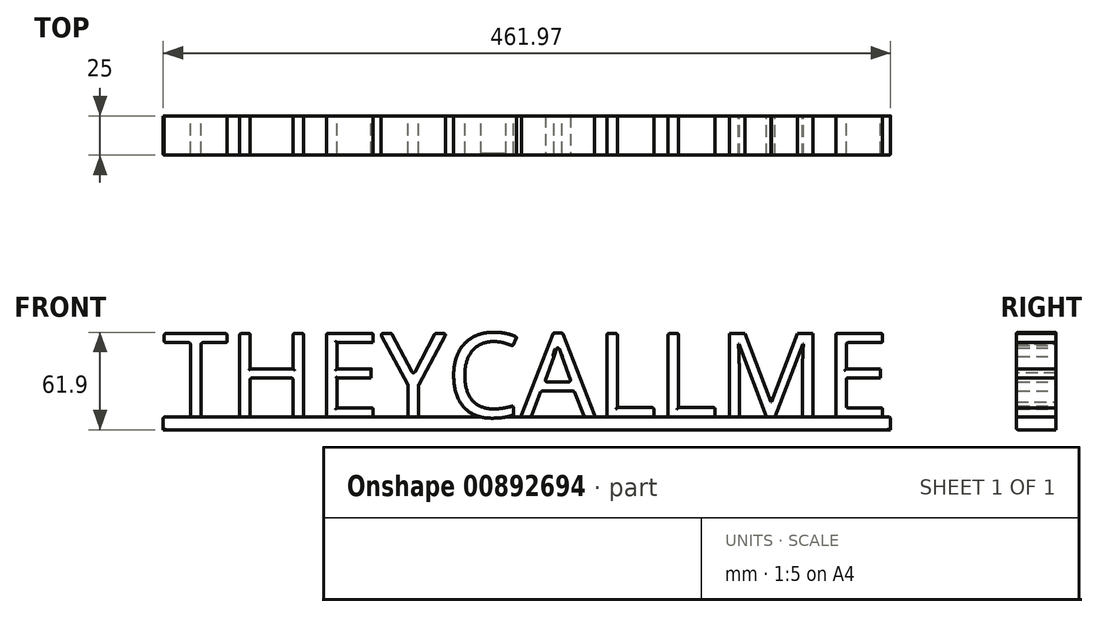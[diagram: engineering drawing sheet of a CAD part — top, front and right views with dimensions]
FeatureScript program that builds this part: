
annotation { "Feature Type Name" : "Feature", "Feature Type Description" : "" }
export const myFeature = defineFeature(function(context is Context, id is Id, definition is map)
    precondition{}
    {
        {
            var Q0;
            Q0=qCreatedBy(makeId("Front.planeOp"),FACE);
            var sketch = newSketch(context, id + "F0", { "sketchPlane" : qUnion([Q0])});
            skText(sketch, "E0", { "text": "THEYCALLME", "fontName": "NotoSans-Regular.ttf"});
            skLineSegment(sketch, "E1.bottom", {"start": v(-74, 3.83) * mm, "end": v(387.97, 3.83) * mm});
            skLineSegment(sketch, "E1.top", {"start": v(-74, -4.21) * mm, "end": v(387.97, -4.21) * mm});
            skLineSegment(sketch, "E1.left", {"start": v(-74, 3.83) * mm, "end": v(-74, -4.21) * mm});
            skLineSegment(sketch, "E1.right", {"start": v(387.97, 3.83) * mm, "end": v(387.97, -4.21) * mm});
            const initialGuessF0  = {"E0": [-0.074, 0.00383, 1, 0, 0.05356]};
            skSetInitialGuess(sketch, initialGuessF0);
            skSolve(sketch);
        }
        {
            var Q0;
            {var subQ0=sQuery(id+"F0.wireOp",EDGE,"E0.sketch_text.stroke-1");Q0=makeQuery(id+"F0.imprint","IMPRINT",FACE,{"disambiguationData":[TD([[makeQuery(id+"F0.imprint","IMPRINT",EDGE,{"derivedFrom":subQ0}),-1.0]])]});}
            var Q1;
            {var subQ0=sQuery(id+"F0.wireOp",EDGE,"E0.sketch_text.stroke-21");Q1=makeQuery(id+"F0.imprint","IMPRINT",FACE,{"disambiguationData":[TD([[makeQuery(id+"F0.imprint","IMPRINT",EDGE,{"derivedFrom":subQ0}),-1.0]])]});}
            var Q2;
            Q2=makeQuery(id+"F0.imprint","IMPRINT",FACE,{"disambiguationData":[TD([[makeQuery(id+"F0.imprint","IMPRINT",EDGE,{"derivedFrom":sQuery(id+"F0.wireOp",EDGE,"E0.sketch_text.stroke-32")}),-1.0]])]});
            var Q3;
            Q3=makeQuery(id+"F0.imprint","IMPRINT",FACE,{"disambiguationData":[TD([[makeQuery(id+"F0.imprint","IMPRINT",EDGE,{"derivedFrom":sQuery(id+"F0.wireOp",EDGE,"E0.sketch_text.stroke-41")}),-1.0]])]});
            var Q4;
            {var subQ0=sQuery(id+"F0.wireOp",EDGE,"E0.sketch_text.stroke-70");Q4=makeQuery(id+"F0.imprint","IMPRINT",FACE,{"disambiguationData":[TD([[makeQuery(id+"F0.imprint","IMPRINT",EDGE,{"derivedFrom":subQ0}),-1.0]])]});}
            var Q5;
            {var subQ1=sQuery(id+"F0.wireOp",EDGE,"E0.sketch_text.stroke-76");Q5=makeQuery(id+"F0.imprint","IMPRINT",FACE,{"disambiguationData":[TD([[makeQuery(id+"F0.imprint","IMPRINT",EDGE,{"derivedFrom":subQ1}),-1.0]])]});}
            var Q6;
            {var subQ1=sQuery(id+"F0.wireOp",EDGE,"E0.sketch_text.stroke-101");Q6=makeQuery(id+"F0.imprint","IMPRINT",FACE,{"disambiguationData":[TD([[makeQuery(id+"F0.imprint","IMPRINT",EDGE,{"derivedFrom":subQ1}),-1.0]])]});}
            var Q7;
            Q7=makeQuery(id+"F0.imprint","IMPRINT",FACE,{"disambiguationData":[TD([[makeQuery(id+"F0.imprint","IMPRINT",EDGE,{"derivedFrom":sQuery(id+"F0.wireOp",EDGE,"E0.sketch_text.stroke-132")}),-1.0]])]});
            var Q8;
            {var subQ1=sQuery(id+"F0.wireOp",EDGE,"E0.sketch_text.stroke-147");Q8=makeQuery(id+"F0.imprint","IMPRINT",FACE,{"disambiguationData":[TD([[makeQuery(id+"F0.imprint","IMPRINT",EDGE,{"derivedFrom":subQ1}),-1.0]])]});}
            var Q9;
            {var subQ1=sQuery(id+"F0.wireOp",EDGE,"E0.sketch_text.stroke-9");Q9=makeQuery(id+"F0.imprint","IMPRINT",FACE,{"disambiguationData":[TD([[makeQuery(id+"F0.imprint","IMPRINT",EDGE,{"derivedFrom":subQ1}),-1.0]])]});}
            var Q10;
            {var subQ0=sQuery(id+"F0.wireOp",EDGE,"E0.sketch_text.stroke-48");Q10=makeQuery(id+"F0.imprint","IMPRINT",FACE,{"disambiguationData":[TD([[makeQuery(id+"F0.imprint","IMPRINT",EDGE,{"derivedFrom":subQ0}),-1.0]])]});}
            var Q11;
            Q11=makeQuery(id+"F0.imprint","IMPRINT",FACE,{"disambiguationData":[TD([[makeQuery(id+"F0.imprint","IMPRINT",EDGE,{"derivedFrom":sQuery(id+"F0.wireOp",EDGE,"E0.sketch_text.stroke-112")}),-1.0]])]});
            var Q12;
            {var subQ0=sQuery(id+"F0.wireOp",EDGE,"E0.sketch_text.stroke-135");var subQ1=sQuery(id+"F0.wireOp",EDGE,"E0.sketch_text.stroke-134");var subQ2=makeQuery(id+"F0.imprint","INTERSECT",VERTEX,{"derivedFrom":[subQ1,subQ0]});Q12=makeQuery(id+"F0.imprint","IMPRINT",FACE,{"disambiguationData":[TD([[makeQuery(id+"F0.imprint","IMPRINT",EDGE,{"disambiguationData":[TD([[subQ2,1.0]])],"derivedFrom":subQ1}),-1.0]])]});}
            var Q13;
            {var subQ2=sQuery(id+"F0.wireOp",EDGE,"E0.sketch_text.stroke-159");Q13=makeQuery(id+"F0.imprint","IMPRINT",FACE,{"disambiguationData":[TD([[makeQuery(id+"F0.imprint","IMPRINT",EDGE,{"derivedFrom":subQ2}),-1.0]])]});}
            var Q14;
            {var subQ3=sQuery(id+"F0.wireOp",EDGE,"E0.sketch_text.stroke-177");Q14=makeQuery(id+"F0.imprint","IMPRINT",FACE,{"disambiguationData":[TD([[makeQuery(id+"F0.imprint","IMPRINT",EDGE,{"derivedFrom":subQ3}),-1.0]])]});}
            var Q15;
            {var subQ1=sQuery(id+"F0.wireOp",EDGE,"E0.sketch_text.stroke-57");Q15=makeQuery(id+"F0.imprint","IMPRINT",FACE,{"disambiguationData":[TD([[makeQuery(id+"F0.imprint","IMPRINT",EDGE,{"derivedFrom":subQ1}),-1.0]])]});}
            var Q16;
            {var subQ1=sQuery(id+"F0.wireOp",EDGE,"E0.sketch_text.stroke-82");Q16=makeQuery(id+"F0.imprint","IMPRINT",FACE,{"disambiguationData":[TD([[makeQuery(id+"F0.imprint","IMPRINT",EDGE,{"derivedFrom":subQ1}),-1.0]])]});}
            var Q17;
            {var subQ1=sQuery(id+"F0.wireOp",EDGE,"E0.sketch_text.stroke-117");Q17=makeQuery(id+"F0.imprint","IMPRINT",FACE,{"disambiguationData":[TD([[makeQuery(id+"F0.imprint","IMPRINT",EDGE,{"derivedFrom":subQ1}),-1.0]])]});}
            extrude(context, id + "F1", {"entities" : qUnion([Q0, Q1, Q2, Q3, Q4, Q5, Q6, Q7, Q8, Q9, Q10, Q11, Q12, Q13, Q14, Q15, Q16, Q17]), "depth" : 25 * mm, "offsetDistance" : 25 * mm});
        }
        {
            var Q0;
            Q0=makeQuery(id+"F1.opExtrude","CAP_FACE",FACE,{"disambiguationData":[OSD([sQuery(id+"F0.wireOp",EDGE,"E0.sketch_text.stroke-1"),sQuery(id+"F0.wireOp",EDGE,"E0.sketch_text.stroke-2"),sQuery(id+"F0.wireOp",EDGE,"E0.sketch_text.stroke-3"),sQuery(id+"F0.wireOp",EDGE,"E0.sketch_text.stroke-4"),sQuery(id+"F0.wireOp",EDGE,"E0.sketch_text.stroke-5"),sQuery(id+"F0.wireOp",EDGE,"E0.sketch_text.stroke-6"),sQuery(id+"F0.wireOp",EDGE,"E0.sketch_text.stroke-7"),sQuery(id+"F0.wireOp",EDGE,"E1.bottom")])],"isStart":false});
            var Q1;
            Q1=makeQuery(id+"F1.opExtrude","CAP_FACE",FACE,{"disambiguationData":[OSD([sQuery(id+"F0.wireOp",EDGE,"E0.sketch_text.stroke-9"),sQuery(id+"F0.wireOp",EDGE,"E0.sketch_text.stroke-10"),sQuery(id+"F0.wireOp",EDGE,"E0.sketch_text.stroke-11"),sQuery(id+"F0.wireOp",EDGE,"E0.sketch_text.stroke-13"),sQuery(id+"F0.wireOp",EDGE,"E0.sketch_text.stroke-14"),sQuery(id+"F0.wireOp",EDGE,"E0.sketch_text.stroke-15"),sQuery(id+"F0.wireOp",EDGE,"E0.sketch_text.stroke-16"),sQuery(id+"F0.wireOp",EDGE,"E0.sketch_text.stroke-17"),sQuery(id+"F0.wireOp",EDGE,"E0.sketch_text.stroke-18"),sQuery(id+"F0.wireOp",EDGE,"E0.sketch_text.stroke-19"),sQuery(id+"F0.wireOp",EDGE,"E1.bottom")])],"isStart":false});
            var Q2;
            Q2=makeQuery(id+"F1.opExtrude","CAP_FACE",FACE,{"disambiguationData":[OSD([sQuery(id+"F0.wireOp",EDGE,"E0.sketch_text.stroke-21"),sQuery(id+"F0.wireOp",EDGE,"E0.sketch_text.stroke-22"),sQuery(id+"F0.wireOp",EDGE,"E0.sketch_text.stroke-23"),sQuery(id+"F0.wireOp",EDGE,"E0.sketch_text.stroke-24"),sQuery(id+"F0.wireOp",EDGE,"E0.sketch_text.stroke-25"),sQuery(id+"F0.wireOp",EDGE,"E0.sketch_text.stroke-26"),sQuery(id+"F0.wireOp",EDGE,"E0.sketch_text.stroke-27"),sQuery(id+"F0.wireOp",EDGE,"E0.sketch_text.stroke-28"),sQuery(id+"F0.wireOp",EDGE,"E0.sketch_text.stroke-29"),sQuery(id+"F0.wireOp",EDGE,"E0.sketch_text.stroke-30"),sQuery(id+"F0.wireOp",EDGE,"E0.sketch_text.stroke-31"),sQuery(id+"F0.wireOp",EDGE,"E1.bottom")])],"isStart":false});
            var Q3;
            Q3=makeQuery(id+"F1.opExtrude","CAP_FACE",FACE,{"disambiguationData":[OSD([sQuery(id+"F0.wireOp",EDGE,"E0.sketch_text.stroke-32"),sQuery(id+"F0.wireOp",EDGE,"E0.sketch_text.stroke-33"),sQuery(id+"F0.wireOp",EDGE,"E0.sketch_text.stroke-34"),sQuery(id+"F0.wireOp",EDGE,"E0.sketch_text.stroke-35"),sQuery(id+"F0.wireOp",EDGE,"E0.sketch_text.stroke-37"),sQuery(id+"F0.wireOp",EDGE,"E0.sketch_text.stroke-38"),sQuery(id+"F0.wireOp",EDGE,"E0.sketch_text.stroke-39"),sQuery(id+"F0.wireOp",EDGE,"E0.sketch_text.stroke-40"),sQuery(id+"F0.wireOp",EDGE,"E1.bottom")])],"isStart":false});
            var Q4;
            Q4=makeQuery(id+"F1.opExtrude","CAP_FACE",FACE,{"disambiguationData":[OSD([sQuery(id+"F0.wireOp",EDGE,"E0.sketch_text.stroke-41"),sQuery(id+"F0.wireOp",EDGE,"E0.sketch_text.stroke-42"),sQuery(id+"F0.wireOp",EDGE,"E0.sketch_text.stroke-43"),sQuery(id+"F0.wireOp",EDGE,"E0.sketch_text.stroke-44"),sQuery(id+"F0.wireOp",EDGE,"E0.sketch_text.stroke-45"),sQuery(id+"F0.wireOp",EDGE,"E0.sketch_text.stroke-46"),sQuery(id+"F0.wireOp",EDGE,"E0.sketch_text.stroke-47"),sQuery(id+"F0.wireOp",EDGE,"E0.sketch_text.stroke-48"),sQuery(id+"F0.wireOp",EDGE,"E0.sketch_text.stroke-49"),sQuery(id+"F0.wireOp",EDGE,"E0.sketch_text.stroke-50"),sQuery(id+"F0.wireOp",EDGE,"E0.sketch_text.stroke-51"),sQuery(id+"F0.wireOp",EDGE,"E0.sketch_text.stroke-52"),sQuery(id+"F0.wireOp",EDGE,"E0.sketch_text.stroke-53"),sQuery(id+"F0.wireOp",EDGE,"E0.sketch_text.stroke-54"),sQuery(id+"F0.wireOp",EDGE,"E0.sketch_text.stroke-55"),sQuery(id+"F0.wireOp",EDGE,"E0.sketch_text.stroke-56")])],"isStart":false});
            var Q5;
            Q5=makeQuery(id+"F1.opExtrude","CAP_FACE",FACE,{"disambiguationData":[OSD([sQuery(id+"F0.wireOp",EDGE,"E0.sketch_text.stroke-57"),sQuery(id+"F0.wireOp",EDGE,"E0.sketch_text.stroke-58"),sQuery(id+"F0.wireOp",EDGE,"E0.sketch_text.stroke-59"),sQuery(id+"F0.wireOp",EDGE,"E0.sketch_text.stroke-61"),sQuery(id+"F0.wireOp",EDGE,"E0.sketch_text.stroke-62"),sQuery(id+"F0.wireOp",EDGE,"E0.sketch_text.stroke-63"),sQuery(id+"F0.wireOp",EDGE,"E0.sketch_text.stroke-65"),sQuery(id+"F0.wireOp",EDGE,"E0.sketch_text.stroke-66"),sQuery(id+"F0.wireOp",EDGE,"E0.sketch_text.stroke-67"),sQuery(id+"F0.wireOp",EDGE,"E0.sketch_text.stroke-68"),sQuery(id+"F0.wireOp",EDGE,"E0.sketch_text.stroke-69"),sQuery(id+"F0.wireOp",EDGE,"E1.bottom")])],"isStart":false});
            var Q6;
            Q6=makeQuery(id+"F1.opExtrude","CAP_FACE",FACE,{"disambiguationData":[OSD([sQuery(id+"F0.wireOp",EDGE,"E0.sketch_text.stroke-70"),sQuery(id+"F0.wireOp",EDGE,"E0.sketch_text.stroke-71"),sQuery(id+"F0.wireOp",EDGE,"E0.sketch_text.stroke-72"),sQuery(id+"F0.wireOp",EDGE,"E0.sketch_text.stroke-73"),sQuery(id+"F0.wireOp",EDGE,"E0.sketch_text.stroke-74"),sQuery(id+"F0.wireOp",EDGE,"E1.bottom")])],"isStart":false});
            var Q7;
            Q7=makeQuery(id+"F1.opExtrude","CAP_FACE",FACE,{"disambiguationData":[OSD([sQuery(id+"F0.wireOp",EDGE,"E0.sketch_text.stroke-76"),sQuery(id+"F0.wireOp",EDGE,"E0.sketch_text.stroke-77"),sQuery(id+"F0.wireOp",EDGE,"E0.sketch_text.stroke-78"),sQuery(id+"F0.wireOp",EDGE,"E0.sketch_text.stroke-79"),sQuery(id+"F0.wireOp",EDGE,"E0.sketch_text.stroke-80"),sQuery(id+"F0.wireOp",EDGE,"E1.bottom")])],"isStart":false});
            var Q8;
            Q8=makeQuery(id+"F1.opExtrude","CAP_FACE",FACE,{"disambiguationData":[OSD([sQuery(id+"F0.wireOp",EDGE,"E0.sketch_text.stroke-82"),sQuery(id+"F0.wireOp",EDGE,"E0.sketch_text.stroke-83"),sQuery(id+"F0.wireOp",EDGE,"E0.sketch_text.stroke-84"),sQuery(id+"F0.wireOp",EDGE,"E0.sketch_text.stroke-85"),sQuery(id+"F0.wireOp",EDGE,"E0.sketch_text.stroke-87"),sQuery(id+"F0.wireOp",EDGE,"E0.sketch_text.stroke-88"),sQuery(id+"F0.wireOp",EDGE,"E0.sketch_text.stroke-89"),sQuery(id+"F0.wireOp",EDGE,"E0.sketch_text.stroke-90"),sQuery(id+"F0.wireOp",EDGE,"E0.sketch_text.stroke-91"),sQuery(id+"F0.wireOp",EDGE,"E0.sketch_text.stroke-92"),sQuery(id+"F0.wireOp",EDGE,"E0.sketch_text.stroke-93"),sQuery(id+"F0.wireOp",EDGE,"E0.sketch_text.stroke-95"),sQuery(id+"F0.wireOp",EDGE,"E0.sketch_text.stroke-96"),sQuery(id+"F0.wireOp",EDGE,"E0.sketch_text.stroke-97"),sQuery(id+"F0.wireOp",EDGE,"E0.sketch_text.stroke-98"),sQuery(id+"F0.wireOp",EDGE,"E1.bottom")])],"isStart":false});
            var Q9;
            Q9=makeQuery(id+"F1.opExtrude","CAP_FACE",FACE,{"disambiguationData":[OSD([sQuery(id+"F0.wireOp",EDGE,"E0.sketch_text.stroke-101"),sQuery(id+"F0.wireOp",EDGE,"E0.sketch_text.stroke-102"),sQuery(id+"F0.wireOp",EDGE,"E0.sketch_text.stroke-103"),sQuery(id+"F0.wireOp",EDGE,"E0.sketch_text.stroke-104"),sQuery(id+"F0.wireOp",EDGE,"E0.sketch_text.stroke-105"),sQuery(id+"F0.wireOp",EDGE,"E0.sketch_text.stroke-106"),sQuery(id+"F0.wireOp",EDGE,"E0.sketch_text.stroke-107"),sQuery(id+"F0.wireOp",EDGE,"E0.sketch_text.stroke-108"),sQuery(id+"F0.wireOp",EDGE,"E0.sketch_text.stroke-109"),sQuery(id+"F0.wireOp",EDGE,"E0.sketch_text.stroke-110"),sQuery(id+"F0.wireOp",EDGE,"E0.sketch_text.stroke-111"),sQuery(id+"F0.wireOp",EDGE,"E1.bottom")])],"isStart":false});
            var Q10;
            Q10=makeQuery(id+"F1.opExtrude","CAP_FACE",FACE,{"disambiguationData":[OSD([sQuery(id+"F0.wireOp",EDGE,"E0.sketch_text.stroke-112"),sQuery(id+"F0.wireOp",EDGE,"E0.sketch_text.stroke-113"),sQuery(id+"F0.wireOp",EDGE,"E0.sketch_text.stroke-114"),sQuery(id+"F0.wireOp",EDGE,"E0.sketch_text.stroke-116"),sQuery(id+"F0.wireOp",EDGE,"E0.sketch_text.stroke-117"),sQuery(id+"F0.wireOp",EDGE,"E0.sketch_text.stroke-118"),sQuery(id+"F0.wireOp",EDGE,"E0.sketch_text.stroke-119"),sQuery(id+"F0.wireOp",EDGE,"E0.sketch_text.stroke-120"),sQuery(id+"F0.wireOp",EDGE,"E0.sketch_text.stroke-121"),sQuery(id+"F0.wireOp",EDGE,"E0.sketch_text.stroke-122"),sQuery(id+"F0.wireOp",EDGE,"E0.sketch_text.stroke-123"),sQuery(id+"F0.wireOp",EDGE,"E0.sketch_text.stroke-124"),sQuery(id+"F0.wireOp",EDGE,"E0.sketch_text.stroke-125"),sQuery(id+"F0.wireOp",EDGE,"E0.sketch_text.stroke-126"),sQuery(id+"F0.wireOp",EDGE,"E0.sketch_text.stroke-127"),sQuery(id+"F0.wireOp",EDGE,"E0.sketch_text.stroke-128"),sQuery(id+"F0.wireOp",EDGE,"E0.sketch_text.stroke-129"),sQuery(id+"F0.wireOp",EDGE,"E0.sketch_text.stroke-130"),sQuery(id+"F0.wireOp",EDGE,"E0.sketch_text.stroke-131"),sQuery(id+"F0.wireOp",EDGE,"E1.top")])],"isStart":false});
            var Q11;
            Q11=makeQuery(id+"F1.opExtrude","CAP_EDGE",EDGE,{"disambiguationData":[OSD([sQuery(id+"F0.wireOp",EDGE,"E0.sketch_text.stroke-141")])],"isStart":false});
            var Q12;
            Q12=makeQuery(id+"F1.opExtrude","CAP_FACE",FACE,{"disambiguationData":[OSD([sQuery(id+"F0.wireOp",EDGE,"E0.sketch_text.stroke-132"),sQuery(id+"F0.wireOp",EDGE,"E0.sketch_text.stroke-133"),sQuery(id+"F0.wireOp",EDGE,"E0.sketch_text.stroke-134"),sQuery(id+"F0.wireOp",EDGE,"E0.sketch_text.stroke-135"),sQuery(id+"F0.wireOp",EDGE,"E0.sketch_text.stroke-136"),sQuery(id+"F0.wireOp",EDGE,"E0.sketch_text.stroke-137"),sQuery(id+"F0.wireOp",EDGE,"E0.sketch_text.stroke-138"),sQuery(id+"F0.wireOp",EDGE,"E0.sketch_text.stroke-139"),sQuery(id+"F0.wireOp",EDGE,"E0.sketch_text.stroke-140"),sQuery(id+"F0.wireOp",EDGE,"E0.sketch_text.stroke-141"),sQuery(id+"F0.wireOp",EDGE,"E0.sketch_text.stroke-142"),sQuery(id+"F0.wireOp",EDGE,"E0.sketch_text.stroke-143"),sQuery(id+"F0.wireOp",EDGE,"E0.sketch_text.stroke-144"),sQuery(id+"F0.wireOp",EDGE,"E0.sketch_text.stroke-145")])],"isStart":false});
            var Q13;
            Q13=makeQuery(id+"F1.opExtrude","CAP_FACE",FACE,{"disambiguationData":[OSD([sQuery(id+"F0.wireOp",EDGE,"E0.sketch_text.stroke-147"),sQuery(id+"F0.wireOp",EDGE,"E0.sketch_text.stroke-148"),sQuery(id+"F0.wireOp",EDGE,"E0.sketch_text.stroke-149"),sQuery(id+"F0.wireOp",EDGE,"E0.sketch_text.stroke-150"),sQuery(id+"F0.wireOp",EDGE,"E0.sketch_text.stroke-151"),sQuery(id+"F0.wireOp",EDGE,"E0.sketch_text.stroke-152"),sQuery(id+"F0.wireOp",EDGE,"E0.sketch_text.stroke-153"),sQuery(id+"F0.wireOp",EDGE,"E0.sketch_text.stroke-154"),sQuery(id+"F0.wireOp",EDGE,"E0.sketch_text.stroke-155"),sQuery(id+"F0.wireOp",EDGE,"E0.sketch_text.stroke-156"),sQuery(id+"F0.wireOp",EDGE,"E0.sketch_text.stroke-157"),sQuery(id+"F0.wireOp",EDGE,"E1.bottom")])],"isStart":false});
            var Q14;
            Q14=makeQuery(id+"F1.opExtrude","CAP_FACE",FACE,{"disambiguationData":[OSD([sQuery(id+"F0.wireOp",EDGE,"E0.sketch_text.stroke-159"),sQuery(id+"F0.wireOp",EDGE,"E0.sketch_text.stroke-160"),sQuery(id+"F0.wireOp",EDGE,"E0.sketch_text.stroke-161"),sQuery(id+"F0.wireOp",EDGE,"E0.sketch_text.stroke-162"),sQuery(id+"F0.wireOp",EDGE,"E0.sketch_text.stroke-163"),sQuery(id+"F0.wireOp",EDGE,"E0.sketch_text.stroke-165"),sQuery(id+"F0.wireOp",EDGE,"E0.sketch_text.stroke-166"),sQuery(id+"F0.wireOp",EDGE,"E0.sketch_text.stroke-167"),sQuery(id+"F0.wireOp",EDGE,"E0.sketch_text.stroke-168"),sQuery(id+"F0.wireOp",EDGE,"E0.sketch_text.stroke-169"),sQuery(id+"F0.wireOp",EDGE,"E0.sketch_text.stroke-170"),sQuery(id+"F0.wireOp",EDGE,"E0.sketch_text.stroke-171"),sQuery(id+"F0.wireOp",EDGE,"E0.sketch_text.stroke-172"),sQuery(id+"F0.wireOp",EDGE,"E0.sketch_text.stroke-173"),sQuery(id+"F0.wireOp",EDGE,"E0.sketch_text.stroke-174"),sQuery(id+"F0.wireOp",EDGE,"E0.sketch_text.stroke-175"),sQuery(id+"F0.wireOp",EDGE,"E1.bottom")])],"isStart":false});
            var Q15;
            Q15=makeQuery(id+"F1.opExtrude","CAP_FACE",FACE,{"disambiguationData":[OSD([sQuery(id+"F0.wireOp",EDGE,"E0.sketch_text.stroke-177"),sQuery(id+"F0.wireOp",EDGE,"E0.sketch_text.stroke-178"),sQuery(id+"F0.wireOp",EDGE,"E0.sketch_text.stroke-179"),sQuery(id+"F0.wireOp",EDGE,"E0.sketch_text.stroke-180"),sQuery(id+"F0.wireOp",EDGE,"E0.sketch_text.stroke-181"),sQuery(id+"F0.wireOp",EDGE,"E0.sketch_text.stroke-183"),sQuery(id+"F0.wireOp",EDGE,"E0.sketch_text.stroke-184"),sQuery(id+"F0.wireOp",EDGE,"E0.sketch_text.stroke-185"),sQuery(id+"F0.wireOp",EDGE,"E0.sketch_text.stroke-186"),sQuery(id+"F0.wireOp",EDGE,"E0.sketch_text.stroke-187"),sQuery(id+"F0.wireOp",EDGE,"E0.sketch_text.stroke-188"),sQuery(id+"F0.wireOp",EDGE,"E0.sketch_text.stroke-189"),sQuery(id+"F0.wireOp",EDGE,"E0.sketch_text.stroke-190"),sQuery(id+"F0.wireOp",EDGE,"E0.sketch_text.stroke-191"),sQuery(id+"F0.wireOp",EDGE,"E0.sketch_text.stroke-192"),sQuery(id+"F0.wireOp",EDGE,"E0.sketch_text.stroke-193"),sQuery(id+"F0.wireOp",EDGE,"E1.bottom")])],"isStart":false});
            var Q16;
            Q16=makeQuery(id+"F1.opExtrude","SWEPT_EDGE",EDGE,{"disambiguationData":[OSD([sQuery(id+"F0.wireOp",EDGE,"E0.sketch_text.stroke-3"),sQuery(id+"F0.wireOp",EDGE,"E0.sketch_text.stroke-4")])]});
            var Q17;
            Q17=makeQuery(id+"F1.opExtrude","SWEPT_EDGE",EDGE,{"disambiguationData":[OSD([sQuery(id+"F0.wireOp",EDGE,"E0.sketch_text.stroke-2"),sQuery(id+"F0.wireOp",EDGE,"E0.sketch_text.stroke-3")])]});
            var Q18;
            Q18=makeQuery(id+"F1.opExtrude","SWEPT_EDGE",EDGE,{"disambiguationData":[OSD([sQuery(id+"F0.wireOp",EDGE,"E0.sketch_text.stroke-1"),sQuery(id+"F0.wireOp",EDGE,"E0.sketch_text.stroke-2")])]});
            var Q19;
            Q19=makeQuery(id+"F1.opExtrude","SWEPT_EDGE",EDGE,{"disambiguationData":[OSD([sQuery(id+"F0.wireOp",EDGE,"E0.sketch_text.stroke-6"),sQuery(id+"F0.wireOp",EDGE,"E0.sketch_text.stroke-7")])]});
            var Q20;
            Q20=makeQuery(id+"F1.opExtrude","SWEPT_EDGE",EDGE,{"disambiguationData":[OSD([sQuery(id+"F0.wireOp",EDGE,"E0.sketch_text.stroke-5"),sQuery(id+"F0.wireOp",EDGE,"E0.sketch_text.stroke-6")])]});
            var Q21;
            Q21=makeQuery(id+"F1.opExtrude","SWEPT_EDGE",EDGE,{"disambiguationData":[OSD([sQuery(id+"F0.wireOp",EDGE,"E0.sketch_text.stroke-4"),sQuery(id+"F0.wireOp",EDGE,"E0.sketch_text.stroke-5")])]});
            var Q22;
            Q22=makeQuery(id+"F1.opExtrude","SWEPT_EDGE",EDGE,{"disambiguationData":[OSD([sQuery(id+"F0.wireOp",EDGE,"E0.sketch_text.stroke-14"),sQuery(id+"F0.wireOp",EDGE,"E0.sketch_text.stroke-15")])]});
            var Q23;
            Q23=makeQuery(id+"F1.opExtrude","SWEPT_EDGE",EDGE,{"disambiguationData":[OSD([sQuery(id+"F0.wireOp",EDGE,"E0.sketch_text.stroke-13"),sQuery(id+"F0.wireOp",EDGE,"E0.sketch_text.stroke-14")])]});
            var Q24;
            Q24=makeQuery(id+"F1.opExtrude","SWEPT_EDGE",EDGE,{"disambiguationData":[OSD([sQuery(id+"F0.wireOp",EDGE,"E0.sketch_text.stroke-17"),sQuery(id+"F0.wireOp",EDGE,"E0.sketch_text.stroke-18")])]});
            var Q25;
            Q25=makeQuery(id+"F1.opExtrude","SWEPT_EDGE",EDGE,{"disambiguationData":[OSD([sQuery(id+"F0.wireOp",EDGE,"E0.sketch_text.stroke-18"),sQuery(id+"F0.wireOp",EDGE,"E0.sketch_text.stroke-19")])]});
            var Q26;
            Q26=makeQuery(id+"F1.opExtrude","SWEPT_EDGE",EDGE,{"disambiguationData":[OSD([sQuery(id+"F0.wireOp",EDGE,"E0.sketch_text.stroke-11"),sQuery(id+"F0.wireOp",EDGE,"E1.bottom")])]});
            var Q27;
            Q27=makeQuery(id+"F1.opExtrude","SWEPT_EDGE",EDGE,{"disambiguationData":[OSD([sQuery(id+"F0.wireOp",EDGE,"E0.sketch_text.stroke-13"),sQuery(id+"F0.wireOp",EDGE,"E1.bottom")])]});
            var Q28;
            Q28=makeQuery(id+"F1.opExtrude","SWEPT_EDGE",EDGE,{"disambiguationData":[OSD([sQuery(id+"F0.wireOp",EDGE,"E0.sketch_text.stroke-7"),sQuery(id+"F0.wireOp",EDGE,"E1.bottom")])]});
            var Q29;
            Q29=makeQuery(id+"F1.opExtrude","SWEPT_EDGE",EDGE,{"disambiguationData":[OSD([sQuery(id+"F0.wireOp",EDGE,"E0.sketch_text.stroke-1"),sQuery(id+"F0.wireOp",EDGE,"E1.bottom")])]});
            var Q30;
            Q30=makeQuery(id+"F1.opExtrude","SWEPT_EDGE",EDGE,{"disambiguationData":[OSD([sQuery(id+"F0.wireOp",EDGE,"E0.sketch_text.stroke-9"),sQuery(id+"F0.wireOp",EDGE,"E1.bottom")])]});
            var Q31;
            Q31=makeQuery(id+"F1.opExtrude","SWEPT_EDGE",EDGE,{"disambiguationData":[OSD([sQuery(id+"F0.wireOp",EDGE,"E0.sketch_text.stroke-19"),sQuery(id+"F0.wireOp",EDGE,"E1.bottom")])]});
            var Q32;
            Q32=makeQuery(id+"F1.opExtrude","SWEPT_EDGE",EDGE,{"disambiguationData":[OSD([sQuery(id+"F0.wireOp",EDGE,"E0.sketch_text.stroke-21"),sQuery(id+"F0.wireOp",EDGE,"E1.bottom")])]});
            var Q33;
            Q33=makeQuery(id+"F1.opExtrude","SWEPT_EDGE",EDGE,{"disambiguationData":[OSD([sQuery(id+"F0.wireOp",EDGE,"E0.sketch_text.stroke-31"),sQuery(id+"F0.wireOp",EDGE,"E1.bottom")])]});
            var Q34;
            Q34=makeQuery(id+"F1.opExtrude","SWEPT_EDGE",EDGE,{"disambiguationData":[OSD([sQuery(id+"F0.wireOp",EDGE,"E0.sketch_text.stroke-21"),sQuery(id+"F0.wireOp",EDGE,"E0.sketch_text.stroke-22")])]});
            var Q35;
            Q35=makeQuery(id+"F1.opExtrude","SWEPT_EDGE",EDGE,{"disambiguationData":[OSD([sQuery(id+"F0.wireOp",EDGE,"E0.sketch_text.stroke-22"),sQuery(id+"F0.wireOp",EDGE,"E0.sketch_text.stroke-23")])]});
            var Q36;
            Q36=makeQuery(id+"F1.opExtrude","SWEPT_EDGE",EDGE,{"disambiguationData":[OSD([sQuery(id+"F0.wireOp",EDGE,"E0.sketch_text.stroke-38"),sQuery(id+"F0.wireOp",EDGE,"E0.sketch_text.stroke-39")])]});
            var Q37;
            Q37=makeQuery(id+"F1.opExtrude","SWEPT_EDGE",EDGE,{"disambiguationData":[OSD([sQuery(id+"F0.wireOp",EDGE,"E0.sketch_text.stroke-39"),sQuery(id+"F0.wireOp",EDGE,"E0.sketch_text.stroke-40")])]});
            var Q38;
            Q38=makeQuery(id+"F1.opExtrude","SWEPT_EDGE",EDGE,{"disambiguationData":[OSD([sQuery(id+"F0.wireOp",EDGE,"E0.sketch_text.stroke-32"),sQuery(id+"F0.wireOp",EDGE,"E0.sketch_text.stroke-33")])]});
            var Q39;
            Q39=makeQuery(id+"F1.opExtrude","SWEPT_EDGE",EDGE,{"disambiguationData":[OSD([sQuery(id+"F0.wireOp",EDGE,"E0.sketch_text.stroke-33"),sQuery(id+"F0.wireOp",EDGE,"E0.sketch_text.stroke-34")])]});
            var Q40;
            Q40=makeQuery(id+"F1.opExtrude","SWEPT_EDGE",EDGE,{"disambiguationData":[OSD([sQuery(id+"F0.wireOp",EDGE,"E0.sketch_text.stroke-32"),sQuery(id+"F0.wireOp",EDGE,"E0.sketch_text.stroke-40")])]});
            var Q41;
            Q41=makeQuery(id+"F1.opExtrude","SWEPT_EDGE",EDGE,{"disambiguationData":[OSD([sQuery(id+"F0.wireOp",EDGE,"E0.sketch_text.stroke-37"),sQuery(id+"F0.wireOp",EDGE,"E0.sketch_text.stroke-38")])]});
            var Q42;
            Q42=makeQuery(id+"F1.opExtrude","SWEPT_EDGE",EDGE,{"disambiguationData":[OSD([sQuery(id+"F0.wireOp",EDGE,"E0.sketch_text.stroke-34"),sQuery(id+"F0.wireOp",EDGE,"E0.sketch_text.stroke-35")])]});
            var Q43;
            Q43=makeQuery(id+"F1.opExtrude","SWEPT_EDGE",EDGE,{"disambiguationData":[OSD([sQuery(id+"F0.wireOp",EDGE,"E0.sketch_text.stroke-37"),sQuery(id+"F0.wireOp",EDGE,"E1.bottom")])]});
            var Q44;
            Q44=makeQuery(id+"F1.opExtrude","SWEPT_EDGE",EDGE,{"disambiguationData":[OSD([sQuery(id+"F0.wireOp",EDGE,"E0.sketch_text.stroke-35"),sQuery(id+"F0.wireOp",EDGE,"E1.bottom")])]});
            var Q45;
            Q45=makeQuery(id+"F1.opExtrude","SWEPT_EDGE",EDGE,{"disambiguationData":[OSD([sQuery(id+"F0.wireOp",EDGE,"E0.sketch_text.stroke-46"),sQuery(id+"F0.wireOp",EDGE,"E0.sketch_text.stroke-47")])]});
            var Q46;
            Q46=makeQuery(id+"F1.opExtrude","SWEPT_EDGE",EDGE,{"disambiguationData":[OSD([sQuery(id+"F0.wireOp",EDGE,"E0.sketch_text.stroke-45"),sQuery(id+"F0.wireOp",EDGE,"E0.sketch_text.stroke-46")])]});
            var Q47;
            Q47=makeQuery(id+"F1.opExtrude","SWEPT_EDGE",EDGE,{"disambiguationData":[OSD([sQuery(id+"F0.wireOp",EDGE,"E0.sketch_text.stroke-55"),sQuery(id+"F0.wireOp",EDGE,"E0.sketch_text.stroke-56")])]});
            var Q48;
            Q48=makeQuery(id+"F1.opExtrude","SWEPT_EDGE",EDGE,{"disambiguationData":[OSD([sQuery(id+"F0.wireOp",EDGE,"E0.sketch_text.stroke-54"),sQuery(id+"F0.wireOp",EDGE,"E0.sketch_text.stroke-55")])]});
            var Q49;
            Q49=makeQuery(id+"F1.opExtrude","SWEPT_EDGE",EDGE,{"disambiguationData":[OSD([sQuery(id+"F0.wireOp",EDGE,"E0.sketch_text.stroke-61"),sQuery(id+"F0.wireOp",EDGE,"E0.sketch_text.stroke-62")])]});
            var Q50;
            Q50=makeQuery(id+"F1.opExtrude","SWEPT_EDGE",EDGE,{"disambiguationData":[OSD([sQuery(id+"F0.wireOp",EDGE,"E0.sketch_text.stroke-62"),sQuery(id+"F0.wireOp",EDGE,"E0.sketch_text.stroke-63")])]});
            var Q51;
            Q51=makeQuery(id+"F1.opExtrude","SWEPT_EDGE",EDGE,{"disambiguationData":[OSD([sQuery(id+"F0.wireOp",EDGE,"E0.sketch_text.stroke-66"),sQuery(id+"F0.wireOp",EDGE,"E0.sketch_text.stroke-67")])]});
            var Q52;
            Q52=makeQuery(id+"F1.opExtrude","SWEPT_EDGE",EDGE,{"disambiguationData":[OSD([sQuery(id+"F0.wireOp",EDGE,"E0.sketch_text.stroke-68"),sQuery(id+"F0.wireOp",EDGE,"E0.sketch_text.stroke-69")])]});
            var Q53;
            Q53=makeQuery(id+"F1.opExtrude","SWEPT_EDGE",EDGE,{"disambiguationData":[OSD([sQuery(id+"F0.wireOp",EDGE,"E0.sketch_text.stroke-65"),sQuery(id+"F0.wireOp",EDGE,"E0.sketch_text.stroke-69")])]});
            var Q54;
            Q54=makeQuery(id+"F1.opExtrude","SWEPT_EDGE",EDGE,{"disambiguationData":[OSD([sQuery(id+"F0.wireOp",EDGE,"E0.sketch_text.stroke-58"),sQuery(id+"F0.wireOp",EDGE,"E0.sketch_text.stroke-59")])]});
            var Q55;
            Q55=makeQuery(id+"F1.opExtrude","SWEPT_EDGE",EDGE,{"disambiguationData":[OSD([sQuery(id+"F0.wireOp",EDGE,"E0.sketch_text.stroke-57"),sQuery(id+"F0.wireOp",EDGE,"E0.sketch_text.stroke-58")])]});
            var Q56;
            Q56=makeQuery(id+"F1.opExtrude","SWEPT_EDGE",EDGE,{"disambiguationData":[OSD([sQuery(id+"F0.wireOp",EDGE,"E0.sketch_text.stroke-57"),sQuery(id+"F0.wireOp",EDGE,"E1.bottom")])]});
            var Q57;
            Q57=makeQuery(id+"F1.opExtrude","SWEPT_EDGE",EDGE,{"disambiguationData":[OSD([sQuery(id+"F0.wireOp",EDGE,"E0.sketch_text.stroke-63"),sQuery(id+"F0.wireOp",EDGE,"E1.bottom")])]});
            var Q58;
            Q58=makeQuery(id+"F1.opExtrude","SWEPT_EDGE",EDGE,{"disambiguationData":[OSD([sQuery(id+"F0.wireOp",EDGE,"E0.sketch_text.stroke-59"),sQuery(id+"F0.wireOp",EDGE,"E1.bottom")])]});
            var Q59;
            Q59=makeQuery(id+"F1.opExtrude","SWEPT_EDGE",EDGE,{"disambiguationData":[OSD([sQuery(id+"F0.wireOp",EDGE,"E0.sketch_text.stroke-61"),sQuery(id+"F0.wireOp",EDGE,"E1.bottom")])]});
            var Q60;
            Q60=makeQuery(id+"F1.opExtrude","SWEPT_EDGE",EDGE,{"disambiguationData":[OSD([sQuery(id+"F0.wireOp",EDGE,"E0.sketch_text.stroke-70"),sQuery(id+"F0.wireOp",EDGE,"E1.bottom")])]});
            var Q61;
            Q61=makeQuery(id+"F1.opExtrude","SWEPT_EDGE",EDGE,{"disambiguationData":[OSD([sQuery(id+"F0.wireOp",EDGE,"E0.sketch_text.stroke-70"),sQuery(id+"F0.wireOp",EDGE,"E0.sketch_text.stroke-71")])]});
            var Q62;
            Q62=makeQuery(id+"F1.opExtrude","SWEPT_EDGE",EDGE,{"disambiguationData":[OSD([sQuery(id+"F0.wireOp",EDGE,"E0.sketch_text.stroke-74"),sQuery(id+"F0.wireOp",EDGE,"E1.bottom")])]});
            var Q63;
            Q63=makeQuery(id+"F1.opExtrude","SWEPT_EDGE",EDGE,{"disambiguationData":[OSD([sQuery(id+"F0.wireOp",EDGE,"E0.sketch_text.stroke-71"),sQuery(id+"F0.wireOp",EDGE,"E0.sketch_text.stroke-72")])]});
            var Q64;
            Q64=makeQuery(id+"F1.opExtrude","SWEPT_EDGE",EDGE,{"disambiguationData":[OSD([sQuery(id+"F0.wireOp",EDGE,"E0.sketch_text.stroke-76"),sQuery(id+"F0.wireOp",EDGE,"E1.bottom")])]});
            var Q65;
            Q65=makeQuery(id+"F1.opExtrude","SWEPT_EDGE",EDGE,{"disambiguationData":[OSD([sQuery(id+"F0.wireOp",EDGE,"E0.sketch_text.stroke-76"),sQuery(id+"F0.wireOp",EDGE,"E0.sketch_text.stroke-77")])]});
            var Q66;
            Q66=makeQuery(id+"F1.opExtrude","SWEPT_EDGE",EDGE,{"disambiguationData":[OSD([sQuery(id+"F0.wireOp",EDGE,"E0.sketch_text.stroke-80"),sQuery(id+"F0.wireOp",EDGE,"E1.bottom")])]});
            var Q67;
            Q67=makeQuery(id+"F1.opExtrude","SWEPT_EDGE",EDGE,{"disambiguationData":[OSD([sQuery(id+"F0.wireOp",EDGE,"E0.sketch_text.stroke-79"),sQuery(id+"F0.wireOp",EDGE,"E0.sketch_text.stroke-80")])]});
            var Q68;
            Q68=makeQuery(id+"F1.opExtrude","SWEPT_EDGE",EDGE,{"disambiguationData":[OSD([sQuery(id+"F0.wireOp",EDGE,"E0.sketch_text.stroke-77"),sQuery(id+"F0.wireOp",EDGE,"E0.sketch_text.stroke-78")])]});
            var Q69;
            Q69=makeQuery(id+"F1.opExtrude","SWEPT_EDGE",EDGE,{"disambiguationData":[OSD([sQuery(id+"F0.wireOp",EDGE,"E0.sketch_text.stroke-87"),sQuery(id+"F0.wireOp",EDGE,"E0.sketch_text.stroke-88")])]});
            var Q70;
            Q70=makeQuery(id+"F1.opExtrude","SWEPT_EDGE",EDGE,{"disambiguationData":[OSD([sQuery(id+"F0.wireOp",EDGE,"E0.sketch_text.stroke-88"),sQuery(id+"F0.wireOp",EDGE,"E0.sketch_text.stroke-89")])]});
            var Q71;
            Q71=makeQuery(id+"F1.opExtrude","SWEPT_EDGE",EDGE,{"disambiguationData":[OSD([sQuery(id+"F0.wireOp",EDGE,"E0.sketch_text.stroke-91"),sQuery(id+"F0.wireOp",EDGE,"E0.sketch_text.stroke-92")])]});
            var Q72;
            Q72=makeQuery(id+"F1.opExtrude","SWEPT_EDGE",EDGE,{"disambiguationData":[OSD([sQuery(id+"F0.wireOp",EDGE,"E0.sketch_text.stroke-92"),sQuery(id+"F0.wireOp",EDGE,"E0.sketch_text.stroke-93")])]});
            var Q73;
            Q73=makeQuery(id+"F1.opExtrude","SWEPT_EDGE",EDGE,{"disambiguationData":[OSD([sQuery(id+"F0.wireOp",EDGE,"E0.sketch_text.stroke-93"),sQuery(id+"F0.wireOp",EDGE,"E1.bottom")])]});
            var Q74;
            Q74=makeQuery(id+"F1.opExtrude","SWEPT_EDGE",EDGE,{"disambiguationData":[OSD([sQuery(id+"F0.wireOp",EDGE,"E0.sketch_text.stroke-95"),sQuery(id+"F0.wireOp",EDGE,"E1.bottom")])]});
            var Q75;
            Q75=makeQuery(id+"F1.opExtrude","SWEPT_EDGE",EDGE,{"disambiguationData":[OSD([sQuery(id+"F0.wireOp",EDGE,"E0.sketch_text.stroke-98"),sQuery(id+"F0.wireOp",EDGE,"E1.bottom")])]});
            var Q76;
            Q76=makeQuery(id+"F1.opExtrude","SWEPT_EDGE",EDGE,{"disambiguationData":[OSD([sQuery(id+"F0.wireOp",EDGE,"E0.sketch_text.stroke-82"),sQuery(id+"F0.wireOp",EDGE,"E1.bottom")])]});
            var Q77;
            Q77=makeQuery(id+"F1.opExtrude","SWEPT_EDGE",EDGE,{"disambiguationData":[OSD([sQuery(id+"F0.wireOp",EDGE,"E0.sketch_text.stroke-85"),sQuery(id+"F0.wireOp",EDGE,"E1.bottom")])]});
            var Q78;
            Q78=makeQuery(id+"F1.opExtrude","SWEPT_EDGE",EDGE,{"disambiguationData":[OSD([sQuery(id+"F0.wireOp",EDGE,"E0.sketch_text.stroke-87"),sQuery(id+"F0.wireOp",EDGE,"E1.bottom")])]});
            var Q79;
            Q79=makeQuery(id+"F1.opExtrude","SWEPT_EDGE",EDGE,{"disambiguationData":[OSD([sQuery(id+"F0.wireOp",EDGE,"E0.sketch_text.stroke-101"),sQuery(id+"F0.wireOp",EDGE,"E1.bottom")])]});
            var Q80;
            Q80=makeQuery(id+"F1.opExtrude","SWEPT_EDGE",EDGE,{"disambiguationData":[OSD([sQuery(id+"F0.wireOp",EDGE,"E0.sketch_text.stroke-101"),sQuery(id+"F0.wireOp",EDGE,"E0.sketch_text.stroke-102")])]});
            var Q81;
            Q81=makeQuery(id+"F1.opExtrude","SWEPT_EDGE",EDGE,{"disambiguationData":[OSD([sQuery(id+"F0.wireOp",EDGE,"E0.sketch_text.stroke-111"),sQuery(id+"F0.wireOp",EDGE,"E1.bottom")])]});
            var Q82;
            Q82=makeQuery(id+"F1.opExtrude","SWEPT_EDGE",EDGE,{"disambiguationData":[OSD([sQuery(id+"F0.wireOp",EDGE,"E0.sketch_text.stroke-108"),sQuery(id+"F0.wireOp",EDGE,"E0.sketch_text.stroke-109")])]});
            var Q83;
            Q83=makeQuery(id+"F1.opExtrude","SWEPT_EDGE",EDGE,{"disambiguationData":[OSD([sQuery(id+"F0.wireOp",EDGE,"E0.sketch_text.stroke-109"),sQuery(id+"F0.wireOp",EDGE,"E0.sketch_text.stroke-110")])]});
            var Q84;
            Q84=makeQuery(id+"F1.opExtrude","SWEPT_EDGE",EDGE,{"disambiguationData":[OSD([sQuery(id+"F0.wireOp",EDGE,"E0.sketch_text.stroke-104"),sQuery(id+"F0.wireOp",EDGE,"E0.sketch_text.stroke-105")])]});
            var Q85;
            Q85=makeQuery(id+"F1.opExtrude","SWEPT_EDGE",EDGE,{"disambiguationData":[OSD([sQuery(id+"F0.wireOp",EDGE,"E0.sketch_text.stroke-103"),sQuery(id+"F0.wireOp",EDGE,"E0.sketch_text.stroke-104")])]});
            var Q86;
            Q86=makeQuery(id+"F1.opExtrude","SWEPT_EDGE",EDGE,{"disambiguationData":[OSD([sQuery(id+"F0.wireOp",EDGE,"E0.sketch_text.stroke-102"),sQuery(id+"F0.wireOp",EDGE,"E0.sketch_text.stroke-103")])]});
            var Q87;
            Q87=makeQuery(id+"F1.opExtrude","SWEPT_EDGE",EDGE,{"disambiguationData":[OSD([sQuery(id+"F0.wireOp",EDGE,"E0.sketch_text.stroke-113"),sQuery(id+"F0.wireOp",EDGE,"E0.sketch_text.stroke-114")])]});
            var Q88;
            Q88=makeQuery(id+"F1.opExtrude","SWEPT_EDGE",EDGE,{"disambiguationData":[OSD([sQuery(id+"F0.wireOp",EDGE,"E0.sketch_text.stroke-138"),sQuery(id+"F0.wireOp",EDGE,"E0.sketch_text.stroke-139")])]});
            var Q89;
            Q89=makeQuery(id+"F1.opExtrude","SWEPT_EDGE",EDGE,{"disambiguationData":[OSD([sQuery(id+"F0.wireOp",EDGE,"E0.sketch_text.stroke-137"),sQuery(id+"F0.wireOp",EDGE,"E0.sketch_text.stroke-138")])]});
            var Q90;
            Q90=makeQuery(id+"F1.opExtrude","SWEPT_EDGE",EDGE,{"disambiguationData":[OSD([sQuery(id+"F0.wireOp",EDGE,"E0.sketch_text.stroke-144"),sQuery(id+"F0.wireOp",EDGE,"E0.sketch_text.stroke-145")])]});
            var Q91;
            Q91=makeQuery(id+"F1.opExtrude","SWEPT_EDGE",EDGE,{"disambiguationData":[OSD([sQuery(id+"F0.wireOp",EDGE,"E0.sketch_text.stroke-132"),sQuery(id+"F0.wireOp",EDGE,"E0.sketch_text.stroke-145")])]});
            var Q92;
            Q92=makeQuery(id+"F1.opExtrude","SWEPT_EDGE",EDGE,{"disambiguationData":[OSD([sQuery(id+"F0.wireOp",EDGE,"E0.sketch_text.stroke-151"),sQuery(id+"F0.wireOp",EDGE,"E0.sketch_text.stroke-152")])]});
            var Q93;
            Q93=makeQuery(id+"F1.opExtrude","SWEPT_EDGE",EDGE,{"disambiguationData":[OSD([sQuery(id+"F0.wireOp",EDGE,"E0.sketch_text.stroke-152"),sQuery(id+"F0.wireOp",EDGE,"E0.sketch_text.stroke-153")])]});
            var Q94;
            Q94=makeQuery(id+"F1.opExtrude","SWEPT_EDGE",EDGE,{"disambiguationData":[OSD([sQuery(id+"F0.wireOp",EDGE,"E0.sketch_text.stroke-153"),sQuery(id+"F0.wireOp",EDGE,"E0.sketch_text.stroke-154")])]});
            var Q95;
            Q95=makeQuery(id+"F1.opExtrude","SWEPT_EDGE",EDGE,{"disambiguationData":[OSD([sQuery(id+"F0.wireOp",EDGE,"E0.sketch_text.stroke-150"),sQuery(id+"F0.wireOp",EDGE,"E0.sketch_text.stroke-151")])]});
            var Q96;
            Q96=makeQuery(id+"F1.opExtrude","SWEPT_EDGE",EDGE,{"disambiguationData":[OSD([sQuery(id+"F0.wireOp",EDGE,"E0.sketch_text.stroke-149"),sQuery(id+"F0.wireOp",EDGE,"E0.sketch_text.stroke-150")])]});
            var Q97;
            Q97=makeQuery(id+"F1.opExtrude","SWEPT_EDGE",EDGE,{"disambiguationData":[OSD([sQuery(id+"F0.wireOp",EDGE,"E0.sketch_text.stroke-154"),sQuery(id+"F0.wireOp",EDGE,"E0.sketch_text.stroke-155")])]});
            var Q98;
            Q98=makeQuery(id+"F1.opExtrude","SWEPT_EDGE",EDGE,{"disambiguationData":[OSD([sQuery(id+"F0.wireOp",EDGE,"E0.sketch_text.stroke-148"),sQuery(id+"F0.wireOp",EDGE,"E0.sketch_text.stroke-149")])]});
            var Q99;
            Q99=makeQuery(id+"F1.opExtrude","SWEPT_EDGE",EDGE,{"disambiguationData":[OSD([sQuery(id+"F0.wireOp",EDGE,"E0.sketch_text.stroke-147"),sQuery(id+"F0.wireOp",EDGE,"E0.sketch_text.stroke-148")])]});
            var Q100;
            Q100=makeQuery(id+"F1.opExtrude","SWEPT_EDGE",EDGE,{"disambiguationData":[OSD([sQuery(id+"F0.wireOp",EDGE,"E0.sketch_text.stroke-147"),sQuery(id+"F0.wireOp",EDGE,"E1.bottom")])]});
            var Q101;
            Q101=makeQuery(id+"F1.opExtrude","SWEPT_EDGE",EDGE,{"disambiguationData":[OSD([sQuery(id+"F0.wireOp",EDGE,"E0.sketch_text.stroke-156"),sQuery(id+"F0.wireOp",EDGE,"E0.sketch_text.stroke-157")])]});
            var Q102;
            Q102=makeQuery(id+"F1.opExtrude","SWEPT_EDGE",EDGE,{"disambiguationData":[OSD([sQuery(id+"F0.wireOp",EDGE,"E0.sketch_text.stroke-157"),sQuery(id+"F0.wireOp",EDGE,"E1.bottom")])]});
            var Q103;
            Q103=makeQuery(id+"F1.opExtrude","SWEPT_EDGE",EDGE,{"disambiguationData":[OSD([sQuery(id+"F0.wireOp",EDGE,"E0.sketch_text.stroke-155"),sQuery(id+"F0.wireOp",EDGE,"E0.sketch_text.stroke-156")])]});
            var Q104;
            Q104=makeQuery(id+"F1.opExtrude","SWEPT_EDGE",EDGE,{"disambiguationData":[OSD([sQuery(id+"F0.wireOp",EDGE,"E0.sketch_text.stroke-166"),sQuery(id+"F0.wireOp",EDGE,"E0.sketch_text.stroke-167")])]});
            var Q105;
            Q105=makeQuery(id+"F1.opExtrude","SWEPT_EDGE",EDGE,{"disambiguationData":[OSD([sQuery(id+"F0.wireOp",EDGE,"E0.sketch_text.stroke-165"),sQuery(id+"F0.wireOp",EDGE,"E0.sketch_text.stroke-166")])]});
            var Q106;
            Q106=makeQuery(id+"F1.opExtrude","SWEPT_EDGE",EDGE,{"disambiguationData":[OSD([sQuery(id+"F0.wireOp",EDGE,"E0.sketch_text.stroke-173"),sQuery(id+"F0.wireOp",EDGE,"E0.sketch_text.stroke-174")])]});
            var Q107;
            Q107=makeQuery(id+"F1.opExtrude","SWEPT_EDGE",EDGE,{"disambiguationData":[OSD([sQuery(id+"F0.wireOp",EDGE,"E0.sketch_text.stroke-174"),sQuery(id+"F0.wireOp",EDGE,"E0.sketch_text.stroke-175")])]});
            var Q108;
            Q108=makeQuery(id+"F1.opExtrude","SWEPT_EDGE",EDGE,{"disambiguationData":[OSD([sQuery(id+"F0.wireOp",EDGE,"E0.sketch_text.stroke-165"),sQuery(id+"F0.wireOp",EDGE,"E1.bottom")])]});
            var Q109;
            Q109=makeQuery(id+"F1.opExtrude","SWEPT_EDGE",EDGE,{"disambiguationData":[OSD([sQuery(id+"F0.wireOp",EDGE,"E0.sketch_text.stroke-163"),sQuery(id+"F0.wireOp",EDGE,"E1.bottom")])]});
            var Q110;
            Q110=makeQuery(id+"F1.opExtrude","SWEPT_EDGE",EDGE,{"disambiguationData":[OSD([sQuery(id+"F0.wireOp",EDGE,"E0.sketch_text.stroke-159"),sQuery(id+"F0.wireOp",EDGE,"E1.bottom")])]});
            var Q111;
            Q111=makeQuery(id+"F1.opExtrude","SWEPT_EDGE",EDGE,{"disambiguationData":[OSD([sQuery(id+"F0.wireOp",EDGE,"E0.sketch_text.stroke-175"),sQuery(id+"F0.wireOp",EDGE,"E1.bottom")])]});
            var Q112;
            Q112=makeQuery(id+"F1.opExtrude","SWEPT_EDGE",EDGE,{"disambiguationData":[OSD([sQuery(id+"F0.wireOp",EDGE,"E0.sketch_text.stroke-181"),sQuery(id+"F0.wireOp",EDGE,"E1.bottom")])]});
            var Q113;
            Q113=makeQuery(id+"F1.opExtrude","SWEPT_EDGE",EDGE,{"disambiguationData":[OSD([sQuery(id+"F0.wireOp",EDGE,"E0.sketch_text.stroke-183"),sQuery(id+"F0.wireOp",EDGE,"E1.bottom")])]});
            var Q114;
            Q114=makeQuery(id+"F1.opExtrude","SWEPT_EDGE",EDGE,{"disambiguationData":[OSD([sQuery(id+"F0.wireOp",EDGE,"E0.sketch_text.stroke-177"),sQuery(id+"F0.wireOp",EDGE,"E1.bottom")])]});
            var Q115;
            Q115=makeQuery(id+"F1.opExtrude","SWEPT_EDGE",EDGE,{"disambiguationData":[OSD([sQuery(id+"F0.wireOp",EDGE,"E0.sketch_text.stroke-193"),sQuery(id+"F0.wireOp",EDGE,"E1.bottom")])]});
            var Q116;
            Q116=makeQuery(id+"F1.opExtrude","SWEPT_EDGE",EDGE,{"disambiguationData":[OSD([sQuery(id+"F0.wireOp",EDGE,"E0.sketch_text.stroke-192"),sQuery(id+"F0.wireOp",EDGE,"E0.sketch_text.stroke-193")])]});
            var Q117;
            Q117=makeQuery(id+"F1.opExtrude","SWEPT_EDGE",EDGE,{"disambiguationData":[OSD([sQuery(id+"F0.wireOp",EDGE,"E0.sketch_text.stroke-191"),sQuery(id+"F0.wireOp",EDGE,"E0.sketch_text.stroke-192")])]});
            var Q118;
            Q118=makeQuery(id+"F1.opExtrude","SWEPT_EDGE",EDGE,{"disambiguationData":[OSD([sQuery(id+"F0.wireOp",EDGE,"E0.sketch_text.stroke-184"),sQuery(id+"F0.wireOp",EDGE,"E0.sketch_text.stroke-185")])]});
            var Q119;
            Q119=makeQuery(id+"F1.opExtrude","SWEPT_EDGE",EDGE,{"disambiguationData":[OSD([sQuery(id+"F0.wireOp",EDGE,"E0.sketch_text.stroke-183"),sQuery(id+"F0.wireOp",EDGE,"E0.sketch_text.stroke-184")])]});
            fillet(context, id + "F2", {"entities" : qUnion([Q0, Q1, Q2, Q3, Q4, Q5, Q6, Q7, Q8, Q9, Q10, Q11, Q12, Q13, Q14, Q15, Q16, Q17, Q18, Q19, Q20, Q21, Q22, Q23, Q24, Q25, Q26, Q27, Q28, Q29, Q30, Q31, Q32, Q33, Q34, Q35, Q36, Q37, Q38, Q39, Q40, Q41, Q42, Q43, Q44, Q45, Q46, Q47, Q48, Q49, Q50, Q51, Q52, Q53, Q54, Q55, Q56, Q57, Q58, Q59, Q60, Q61, Q62, Q63, Q64, Q65, Q66, Q67, Q68, Q69, Q70, Q71, Q72, Q73, Q74, Q75, Q76, Q77, Q78, Q79, Q80, Q81, Q82, Q83, Q84, Q85, Q86, Q87, Q88, Q89, Q90, Q91, Q92, Q93, Q94, Q95, Q96, Q97, Q98, Q99, Q100, Q101, Q102, Q103, Q104, Q105, Q106, Q107, Q108, Q109, Q110, Q111, Q112, Q113, Q114, Q115, Q116, Q117, Q118, Q119]), "tangentPropagation" : true, "radius" : 1 * mm, "defaultsChanged" : false, "vertexSettings" : [], "allowEdgeOverflow" : false});
        }
        {
            var Q0;
            {var subQ16=sQuery(id+"F0.wireOp",EDGE,"E0.sketch_text.stroke-48");Q0=makeQuery(id+"F0.imprint","IMPRINT",FACE,{"disambiguationData":[TD([[makeQuery(id+"F0.imprint","IMPRINT",EDGE,{"derivedFrom":subQ16}),1.0]])]});}
            var Q1;
            {var subQ20=sQuery(id+"F0.wireOp",EDGE,"E1.right");Q1=makeQuery(id+"F0.imprint","IMPRINT",FACE,{"disambiguationData":[TD([[makeQuery(id+"F0.imprint","IMPRINT",EDGE,{"derivedFrom":subQ20}),-1.0]])]});}
            extrude(context, id + "F3", {"entities" : qUnion([Q0, Q1]), "operationType" : NewBodyOperationType.ADD, "depth" : 25 * mm, "offsetDistance" : 25 * mm});
        }
        {
            var Q0;
            {var subQ0=sQuery(id+"F0.wireOp",EDGE,"E1.bottom");var subQ1=makeQuery(id+"F0.imprint","INTERSECT",VERTEX,{"derivedFrom":[sQuery(id+"F0.wireOp",EDGE,"E0.sketch_text.stroke-35"),subQ0]});var subQ3=makeQuery(id+"F0.imprint","INTERSECT",VERTEX,{"derivedFrom":[sQuery(id+"F0.wireOp",EDGE,"E0.sketch_text.stroke-31"),subQ0]});var subQ4=makeQuery(id+"F0.imprint","INTERSECT",VERTEX,{"derivedFrom":[sQuery(id+"F0.wireOp",EDGE,"E0.sketch_text.stroke-21"),subQ0]});var subQ5=makeQuery(id+"F0.imprint","INTERSECT",VERTEX,{"derivedFrom":[sQuery(id+"F0.wireOp",EDGE,"E0.sketch_text.stroke-19"),subQ0]});var subQ6=makeQuery(id+"F0.imprint","INTERSECT",VERTEX,{"derivedFrom":[sQuery(id+"F0.wireOp",EDGE,"E0.sketch_text.stroke-9"),subQ0]});var subQ7=makeQuery(id+"F0.imprint","INTERSECT",VERTEX,{"derivedFrom":[sQuery(id+"F0.wireOp",EDGE,"E0.sketch_text.stroke-11"),subQ0]});var subQ9=makeQuery(id+"F0.imprint","INTERSECT",VERTEX,{"derivedFrom":[sQuery(id+"F0.wireOp",EDGE,"E0.sketch_text.stroke-7"),subQ0]});var subQ10=makeQuery(id+"F0.imprint","INTERSECT",VERTEX,{"derivedFrom":[sQuery(id+"F0.wireOp",EDGE,"E0.sketch_text.stroke-1"),subQ0]});Q0=makeQuery(id+"F3.opExtrude","CAP_EDGE",EDGE,{"disambiguationData":[OSD([subQ0]),TDD([makeQuery(id+"F0.imprint","IMPRINT",EDGE,{"disambiguationData":[TD([[subQ10,1.0]])],"derivedFrom":subQ0}),makeQuery(id+"F0.imprint","IMPRINT",EDGE,{"disambiguationData":[TD([[subQ10,-1.0]])],"derivedFrom":subQ0}),makeQuery(id+"F0.imprint","IMPRINT",EDGE,{"disambiguationData":[TD([[subQ9,-1.0]])],"derivedFrom":subQ0}),makeQuery(id+"F0.imprint","IMPRINT",EDGE,{"disambiguationData":[TD([[subQ7,1.0]])],"derivedFrom":subQ0}),makeQuery(id+"F0.imprint","IMPRINT",EDGE,{"disambiguationData":[TD([[subQ6,1.0]])],"derivedFrom":subQ0}),makeQuery(id+"F0.imprint","IMPRINT",EDGE,{"disambiguationData":[TD([[subQ6,-1.0]])],"derivedFrom":subQ0}),makeQuery(id+"F0.imprint","IMPRINT",EDGE,{"disambiguationData":[TD([[subQ5,-1.0]])],"derivedFrom":subQ0}),makeQuery(id+"F0.imprint","IMPRINT",EDGE,{"disambiguationData":[TD([[subQ4,-1.0]])],"derivedFrom":subQ0}),makeQuery(id+"F0.imprint","IMPRINT",EDGE,{"disambiguationData":[TD([[subQ3,-1.0]])],"derivedFrom":subQ0}),makeQuery(id+"F0.imprint","IMPRINT",EDGE,{"disambiguationData":[TD([[subQ1,1.0]])],"derivedFrom":subQ0}),makeQuery(id+"F0.imprint","IMPRINT",EDGE,{"disambiguationData":[TD([[subQ1,-1.0]])],"derivedFrom":subQ0})])],"isStart":false});}
            var Q1;
            {var subQ0=sQuery(id+"F0.wireOp",EDGE,"E1.bottom");var subQ1=makeQuery(id+"F0.imprint","INTERSECT",VERTEX,{"derivedFrom":[sQuery(id+"F0.wireOp",EDGE,"E0.sketch_text.stroke-111"),subQ0]});var subQ2=makeQuery(id+"F0.imprint","INTERSECT",VERTEX,{"derivedFrom":[sQuery(id+"F0.wireOp",EDGE,"E0.sketch_text.stroke-101"),subQ0]});var subQ3=makeQuery(id+"F0.imprint","INTERSECT",VERTEX,{"derivedFrom":[sQuery(id+"F0.wireOp",EDGE,"E0.sketch_text.stroke-93"),subQ0]});var subQ4=makeQuery(id+"F0.imprint","INTERSECT",VERTEX,{"derivedFrom":[sQuery(id+"F0.wireOp",EDGE,"E0.sketch_text.stroke-95"),subQ0]});var subQ6=makeQuery(id+"F0.imprint","INTERSECT",VERTEX,{"derivedFrom":[sQuery(id+"F0.wireOp",EDGE,"E0.sketch_text.stroke-82"),subQ0]});var subQ7=makeQuery(id+"F0.imprint","INTERSECT",VERTEX,{"derivedFrom":[sQuery(id+"F0.wireOp",EDGE,"E0.sketch_text.stroke-85"),subQ0]});var subQ9=makeQuery(id+"F0.imprint","INTERSECT",VERTEX,{"derivedFrom":[sQuery(id+"F0.wireOp",EDGE,"E0.sketch_text.stroke-80"),subQ0]});var subQ10=makeQuery(id+"F0.imprint","INTERSECT",VERTEX,{"derivedFrom":[sQuery(id+"F0.wireOp",EDGE,"E0.sketch_text.stroke-76"),subQ0]});var subQ11=makeQuery(id+"F0.imprint","INTERSECT",VERTEX,{"derivedFrom":[sQuery(id+"F0.wireOp",EDGE,"E0.sketch_text.stroke-74"),subQ0]});var subQ12=makeQuery(id+"F0.imprint","INTERSECT",VERTEX,{"derivedFrom":[sQuery(id+"F0.wireOp",EDGE,"E0.sketch_text.stroke-70"),subQ0]});var subQ13=makeQuery(id+"F0.imprint","INTERSECT",VERTEX,{"derivedFrom":[sQuery(id+"F0.wireOp",EDGE,"E0.sketch_text.stroke-63"),subQ0]});var subQ14=makeQuery(id+"F0.imprint","INTERSECT",VERTEX,{"derivedFrom":[sQuery(id+"F0.wireOp",EDGE,"E0.sketch_text.stroke-57"),subQ0]});var subQ15=makeQuery(id+"F0.imprint","INTERSECT",VERTEX,{"derivedFrom":[sQuery(id+"F0.wireOp",EDGE,"E0.sketch_text.stroke-59"),subQ0]});var subQ16=makeQuery(id+"F0.imprint","INTERSECT",VERTEX,{"derivedFrom":[sQuery(id+"F0.wireOp",EDGE,"E0.sketch_text.stroke-61"),subQ0]});Q1=makeQuery(id+"F3.opExtrude","CAP_EDGE",EDGE,{"disambiguationData":[OSD([subQ0]),TDD([makeQuery(id+"F0.imprint","IMPRINT",EDGE,{"disambiguationData":[TD([[subQ16,1.0]])],"derivedFrom":subQ0}),makeQuery(id+"F0.imprint","IMPRINT",EDGE,{"disambiguationData":[TD([[subQ15,1.0]])],"derivedFrom":subQ0}),makeQuery(id+"F0.imprint","IMPRINT",EDGE,{"disambiguationData":[TD([[subQ14,1.0]])],"derivedFrom":subQ0}),makeQuery(id+"F0.imprint","IMPRINT",EDGE,{"disambiguationData":[TD([[subQ14,-1.0]])],"derivedFrom":subQ0}),makeQuery(id+"F0.imprint","IMPRINT",EDGE,{"disambiguationData":[TD([[subQ13,-1.0]])],"derivedFrom":subQ0}),makeQuery(id+"F0.imprint","IMPRINT",EDGE,{"disambiguationData":[TD([[subQ12,-1.0]])],"derivedFrom":subQ0}),makeQuery(id+"F0.imprint","IMPRINT",EDGE,{"disambiguationData":[TD([[subQ11,-1.0]])],"derivedFrom":subQ0}),makeQuery(id+"F0.imprint","IMPRINT",EDGE,{"disambiguationData":[TD([[subQ10,-1.0]])],"derivedFrom":subQ0}),makeQuery(id+"F0.imprint","IMPRINT",EDGE,{"disambiguationData":[TD([[subQ9,-1.0]])],"derivedFrom":subQ0}),makeQuery(id+"F0.imprint","IMPRINT",EDGE,{"disambiguationData":[TD([[subQ7,1.0]])],"derivedFrom":subQ0}),makeQuery(id+"F0.imprint","IMPRINT",EDGE,{"disambiguationData":[TD([[subQ6,1.0]])],"derivedFrom":subQ0}),makeQuery(id+"F0.imprint","IMPRINT",EDGE,{"disambiguationData":[TD([[subQ6,-1.0]])],"derivedFrom":subQ0}),makeQuery(id+"F0.imprint","IMPRINT",EDGE,{"disambiguationData":[TD([[subQ4,1.0]])],"derivedFrom":subQ0}),makeQuery(id+"F0.imprint","IMPRINT",EDGE,{"disambiguationData":[TD([[subQ3,1.0]])],"derivedFrom":subQ0}),makeQuery(id+"F0.imprint","IMPRINT",EDGE,{"disambiguationData":[TD([[subQ3,-1.0]])],"derivedFrom":subQ0}),makeQuery(id+"F0.imprint","IMPRINT",EDGE,{"disambiguationData":[TD([[subQ2,-1.0]])],"derivedFrom":subQ0}),makeQuery(id+"F0.imprint","IMPRINT",EDGE,{"disambiguationData":[TD([[subQ1,-1.0]])],"derivedFrom":subQ0})])],"isStart":false});}
            var Q2;
            {var subQ0=sQuery(id+"F0.wireOp",EDGE,"E1.top");Q2=makeQuery(id+"F3.opExtrude","CAP_EDGE",EDGE,{"disambiguationData":[OSD([subQ0]),TDD([makeQuery(id+"F0.imprint","IMPRINT",EDGE,{"disambiguationData":[TD([[makeQuery(id+"F0.imprint","INTERSECT",VERTEX,{"derivedFrom":[subQ0,sQuery(id+"F0.wireOp",EDGE,"E1.left")]}),-1.0]])],"derivedFrom":subQ0})])],"isStart":false});}
            var Q3;
            Q3=makeQuery(id+"F3.opExtrude","CAP_EDGE",EDGE,{"disambiguationData":[OSD([sQuery(id+"F0.wireOp",EDGE,"E1.left")])],"isStart":false});
            var Q4;
            Q4=makeQuery(id+"F3.opExtrude","SWEPT_EDGE",EDGE,{"disambiguationData":[OSD([sQuery(id+"F0.wireOp",EDGE,"E1.bottom"),sQuery(id+"F0.wireOp",EDGE,"E1.left")])]});
            var Q5;
            Q5=makeQuery(id+"F3.opExtrude","CAP_EDGE",EDGE,{"disambiguationData":[OSD([sQuery(id+"F0.wireOp",EDGE,"E0.sketch_text.stroke-116")])],"isStart":false});
            var Q6;
            Q6=makeQuery(id+"F3.opExtrude","CAP_EDGE",EDGE,{"disambiguationData":[OSD([sQuery(id+"F0.wireOp",EDGE,"E0.sketch_text.stroke-114")])],"isStart":false});
            var Q7;
            {var subQ0=sQuery(id+"F0.wireOp",EDGE,"E1.bottom");Q7=makeQuery(id+"F3.opExtrude","CAP_EDGE",EDGE,{"disambiguationData":[OSD([subQ0]),TDD([makeQuery(id+"F0.imprint","IMPRINT",EDGE,{"disambiguationData":[TD([[makeQuery(id+"F0.imprint","INTERSECT",VERTEX,{"derivedFrom":[sQuery(id+"F0.wireOp",EDGE,"E0.sketch_text.stroke-114"),subQ0]}),-1.0]])],"derivedFrom":subQ0})])],"isStart":false});}
            var Q8;
            {var subQ0=sQuery(id+"F0.wireOp",EDGE,"E1.bottom");var subQ1=makeQuery(id+"F0.imprint","INTERSECT",VERTEX,{"derivedFrom":[sQuery(id+"F0.wireOp",EDGE,"E0.sketch_text.stroke-193"),subQ0]});var subQ2=makeQuery(id+"F0.imprint","INTERSECT",VERTEX,{"derivedFrom":[sQuery(id+"F0.wireOp",EDGE,"E0.sketch_text.stroke-177"),subQ0]});var subQ3=makeQuery(id+"F0.imprint","INTERSECT",VERTEX,{"derivedFrom":[sQuery(id+"F0.wireOp",EDGE,"E0.sketch_text.stroke-181"),subQ0]});var subQ5=makeQuery(id+"F0.imprint","INTERSECT",VERTEX,{"derivedFrom":[sQuery(id+"F0.wireOp",EDGE,"E0.sketch_text.stroke-175"),subQ0]});var subQ6=makeQuery(id+"F0.imprint","INTERSECT",VERTEX,{"derivedFrom":[sQuery(id+"F0.wireOp",EDGE,"E0.sketch_text.stroke-159"),subQ0]});var subQ7=makeQuery(id+"F0.imprint","INTERSECT",VERTEX,{"derivedFrom":[sQuery(id+"F0.wireOp",EDGE,"E0.sketch_text.stroke-163"),subQ0]});var subQ9=makeQuery(id+"F0.imprint","INTERSECT",VERTEX,{"derivedFrom":[sQuery(id+"F0.wireOp",EDGE,"E0.sketch_text.stroke-157"),subQ0]});var subQ10=makeQuery(id+"F0.imprint","INTERSECT",VERTEX,{"derivedFrom":[sQuery(id+"F0.wireOp",EDGE,"E0.sketch_text.stroke-147"),subQ0]});Q8=makeQuery(id+"F3.opExtrude","CAP_EDGE",EDGE,{"disambiguationData":[OSD([subQ0]),TDD([makeQuery(id+"F0.imprint","IMPRINT",EDGE,{"disambiguationData":[TD([[subQ10,1.0]])],"derivedFrom":subQ0}),makeQuery(id+"F0.imprint","IMPRINT",EDGE,{"disambiguationData":[TD([[subQ10,-1.0]])],"derivedFrom":subQ0}),makeQuery(id+"F0.imprint","IMPRINT",EDGE,{"disambiguationData":[TD([[subQ9,-1.0]])],"derivedFrom":subQ0}),makeQuery(id+"F0.imprint","IMPRINT",EDGE,{"disambiguationData":[TD([[subQ7,1.0]])],"derivedFrom":subQ0}),makeQuery(id+"F0.imprint","IMPRINT",EDGE,{"disambiguationData":[TD([[subQ6,1.0]])],"derivedFrom":subQ0}),makeQuery(id+"F0.imprint","IMPRINT",EDGE,{"disambiguationData":[TD([[subQ6,-1.0]])],"derivedFrom":subQ0}),makeQuery(id+"F0.imprint","IMPRINT",EDGE,{"disambiguationData":[TD([[subQ5,-1.0]])],"derivedFrom":subQ0}),makeQuery(id+"F0.imprint","IMPRINT",EDGE,{"disambiguationData":[TD([[subQ3,1.0]])],"derivedFrom":subQ0}),makeQuery(id+"F0.imprint","IMPRINT",EDGE,{"disambiguationData":[TD([[subQ2,1.0]])],"derivedFrom":subQ0}),makeQuery(id+"F0.imprint","IMPRINT",EDGE,{"disambiguationData":[TD([[subQ2,-1.0]])],"derivedFrom":subQ0}),makeQuery(id+"F0.imprint","IMPRINT",EDGE,{"disambiguationData":[TD([[subQ1,-1.0]])],"derivedFrom":subQ0})])],"isStart":false});}
            var Q9;
            Q9=makeQuery(id+"F3.opExtrude","CAP_EDGE",EDGE,{"disambiguationData":[OSD([sQuery(id+"F0.wireOp",EDGE,"E1.right")])],"isStart":false});
            var Q10;
            Q10=makeQuery(id+"F3.opExtrude","SWEPT_EDGE",EDGE,{"disambiguationData":[OSD([sQuery(id+"F0.wireOp",EDGE,"E1.bottom"),sQuery(id+"F0.wireOp",EDGE,"E1.right")])]});
            fillet(context, id + "F4", {"entities" : qUnion([Q0, Q1, Q2, Q3, Q4, Q5, Q6, Q7, Q8, Q9, Q10]), "tangentPropagation" : true, "radius" : 1 * mm, "defaultsChanged" : false, "vertexSettings" : [], "allowEdgeOverflow" : false});
        }
    });
